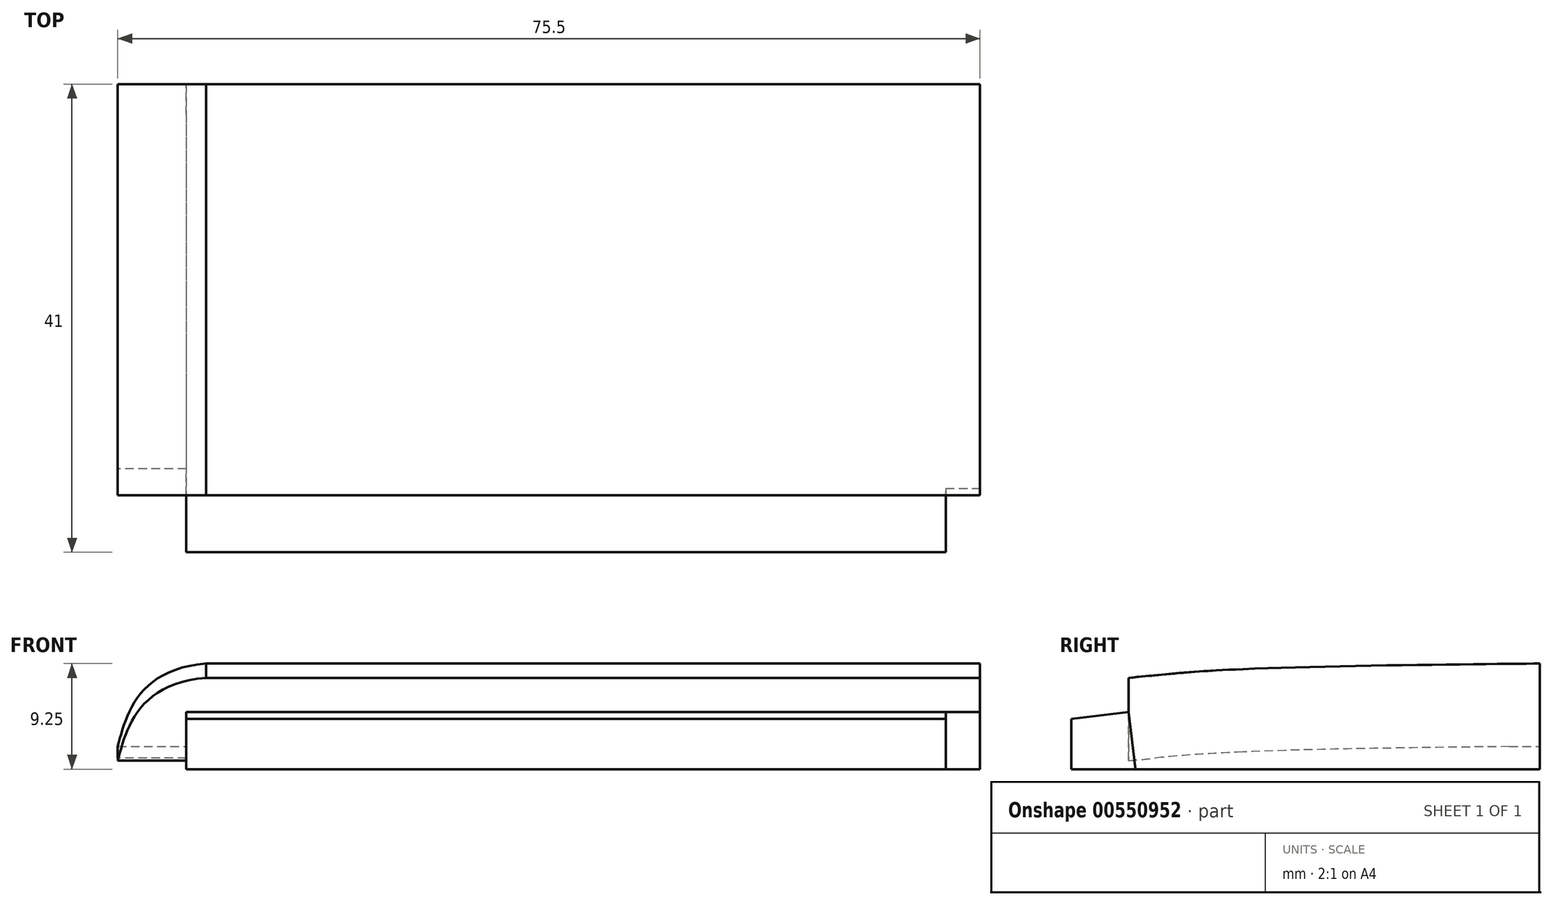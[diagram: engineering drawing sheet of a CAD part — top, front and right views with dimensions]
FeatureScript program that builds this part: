
annotation { "Feature Type Name" : "Feature", "Feature Type Description" : "" }
export const myFeature = defineFeature(function(context is Context, id is Id, definition is map)
    precondition{}
    {
        {
            var Q0;
            Q0=qCreatedBy(makeId("Right.planeOp"),FACE);
            var sketch = newSketch(context, id + "F0", { "sketchPlane" : qUnion([Q0])});
            skLineSegment(sketch, "E0", {"start": v(18, 0) * mm, "end": v(-18, 0) * mm});
            skLineSegment(sketch, "E1", {"start": v(18, 0) * mm, "end": v(18, 3) * mm});
            skLineSegment(sketch, "E2", {"start": v(-18, 0) * mm, "end": v(-18, 3) * mm});
            skLineSegment(sketch, "E3", {"start": v(-8, 0) * mm, "end": v(-8, 3.76) * mm});
            skLineSegment(sketch, "E4", {"start": v(18, 3) * mm, "end": v(18, 4.25) * mm});
            skFitSpline(sketch, "E5", {"points": [v(-18, 3) * mm, v(-8, 3.76) * mm, v(18, 4.25) * mm], "startDerivative": vector(22.72, 2.06) * mm, "endDerivative": vector(17.15, 0.15) * mm});
            skLineSegment(sketch, "E6.bottom", {"start": v(18, 0) * mm, "end": v(-23, 0) * mm});
            skLineSegment(sketch, "E6.top", {"start": v(18, -5) * mm, "end": v(-23, -5) * mm});
            skLineSegment(sketch, "E6.left", {"start": v(18, 0) * mm, "end": v(18, -5) * mm});
            skLineSegment(sketch, "E6.right", {"start": v(-23, 0) * mm, "end": v(-23, -5) * mm});
            skLineSegment(sketch, "E7", {"start": v(-18, 0) * mm, "end": v(-23, -0.6) * mm});
            skSolve(sketch);
        }
        {
            var Q0;
            {var subQ1=sQuery(id+"F0.wireOp",EDGE,"E1");Q0=makeQuery(id+"F0.imprint","IMPRINT",FACE,{"disambiguationData":[TD([[makeQuery(id+"F0.imprint","IMPRINT",EDGE,{"derivedFrom":subQ1}),1.0]])]});}
            var Q1;
            {var subQ0=sQuery(id+"F0.wireOp",EDGE,"E2");Q1=makeQuery(id+"F0.imprint","IMPRINT",FACE,{"disambiguationData":[TD([[makeQuery(id+"F0.imprint","IMPRINT",EDGE,{"derivedFrom":subQ0}),-1.0]])]});}
            var Q2;
            {var subQ1=sQuery(id+"F0.wireOp",EDGE,"E6.top");Q2=makeQuery(id+"F0.imprint","IMPRINT",FACE,{"disambiguationData":[TD([[makeQuery(id+"F0.imprint","IMPRINT",EDGE,{"derivedFrom":subQ1}),-1.0]])]});}
            extrude(context, id + "F1", {"entities" : qUnion([Q0, Q1, Q2]), "endBound" : BoundingType.SYMMETRIC, "depth" : 75.5 * mm, "offsetDistance" : 25 * mm});
        }
        {
            var Q0;
            Q0=makeQuery(id+"F1.opExtrude","SWEPT_FACE",FACE,{"disambiguationData":[OSD([sQuery(id+"F0.wireOp",EDGE,"E1"),sQuery(id+"F0.wireOp",EDGE,"E4"),sQuery(id+"F0.wireOp",EDGE,"E6.left")])]});
            var sketch = newSketch(context, id + "F2", { "sketchPlane" : qUnion([Q0])});
            skLineSegment(sketch, "E8.0", {"start": v(37.75, -5) * mm, "end": v(37.75, 4.25) * mm});
            skLineSegment(sketch, "E9.0", {"start": v(-37.75, 4.25) * mm, "end": v(37.75, 4.25) * mm});
            skPoint(sketch, "E10", {"position": v(30, 4.25) * mm});
            skPoint(sketch, "E11", {"position": v(37.75, -3) * mm});
            skFitSpline(sketch, "E12", {"points": [v(30, 4.25) * mm, v(37.75, -3) * mm], "startDerivative": vector(18.2, -1.34) * mm, "endDerivative": vector(2.03, -7.72) * mm});
            skSolve(sketch);
        }
        {
            var Q0;
            {var subQ3=sQuery(id+"F2.wireOp",EDGE,"E12");Q0=makeQuery(id+"F2.imprint","IMPRINT",FACE,{"disambiguationData":[TD([[makeQuery(id+"F2.imprint","IMPRINT",EDGE,{"derivedFrom":subQ3}),1.0]])]});}
            var Q1;
            Q1=makeQuery(id+"F1.opExtrude","CAP_EDGE",EDGE,{"disambiguationData":[OSD([sQuery(id+"F0.wireOp",EDGE,"E5")])],"isStart":true});
            sweep(context, id + "F3", {"operationType" : NewBodyOperationType.REMOVE, "profiles" : qUnion([Q0]), "path" : qUnion([Q1]), "keepProfileOrientation" : true});
        }
        {
            var Q0;
            Q0=makeQuery(id+"F1.opExtrude","CAP_FACE",FACE,{"disambiguationData":[OSD([sQuery(id+"F0.wireOp",EDGE,"E1"),sQuery(id+"F0.wireOp",EDGE,"E2"),sQuery(id+"F0.wireOp",EDGE,"E4"),sQuery(id+"F0.wireOp",EDGE,"E5"),sQuery(id+"F0.wireOp",EDGE,"E6.top"),sQuery(id+"F0.wireOp",EDGE,"E6.left"),sQuery(id+"F0.wireOp",EDGE,"E6.right"),sQuery(id+"F0.wireOp",EDGE,"E7")])],"isStart":true});
            var sketch = newSketch(context, id + "F4", { "sketchPlane" : qUnion([Q0])});
            skLineSegment(sketch, "E13.0.0", {"start": v(23, -0.6) * mm, "end": v(18, 0) * mm});
            skLineSegment(sketch, "E13.0.1", {"start": v(18, 0) * mm, "end": v(18, -4.25) * mm});
            skFitSpline(sketch, "E13.0.2", {"points": [v(18, -4.25) * mm, v(16.1, -4.08) * mm, v(14.5, -3.9) * mm, v(11.13, -3.65) * mm, v(9.86, -3.57) * mm, v(6.75, -3.43) * mm, v(4.92, -3.37) * mm, v(-4.98, -3.11) * mm, v(-15.14, -3.03) * mm, v(-18, -3) * mm]});
            skLineSegment(sketch, "E13.0.3", {"start": v(-18, -3) * mm, "end": v(-18, -5) * mm});
            skLineSegment(sketch, "E13.0.4", {"start": v(-18, -5) * mm, "end": v(23, -5) * mm});
            skLineSegment(sketch, "E13.0.5", {"start": v(23, -5) * mm, "end": v(23, -0.6) * mm});
            skSolve(sketch);
        }
        {
            var Q0;
            Q0=makeQuery(id+"F4.imprint","IMPRINT",FACE,{"disambiguationData":[TD([[makeQuery(id+"F4.imprint","IMPRINT",EDGE,{"derivedFrom":sQuery(id+"F4.wireOp",EDGE,"E13.0.0")}),-1.0]])]});
            extrude(context, id + "F5", {"entities" : qUnion([Q0]), "operationType" : NewBodyOperationType.REMOVE, "oppositeDirection" : true, "depth" : 6 * mm, "offsetDistance" : 25 * mm});
        }
        {
            var Q0;
            Q0=makeQuery(id+"F1.opExtrude","SWEPT_FACE",FACE,{"disambiguationData":[OSD([sQuery(id+"F0.wireOp",EDGE,"E7")])]});
            var sketch = newSketch(context, id + "F6", { "sketchPlane" : qUnion([Q0])});
            skLineSegment(sketch, "E14.bottom", {"start": v(37.75, -17.87) * mm, "end": v(34.75, -17.87) * mm});
            skLineSegment(sketch, "E14.top", {"start": v(37.75, -22.9) * mm, "end": v(34.75, -22.9) * mm});
            skLineSegment(sketch, "E14.left", {"start": v(37.75, -17.87) * mm, "end": v(37.75, -22.9) * mm});
            skLineSegment(sketch, "E14.right", {"start": v(34.75, -17.87) * mm, "end": v(34.75, -22.9) * mm});
            skSolve(sketch);
        }
        {
            var Q0;
            Q0=makeQuery(id+"F6.imprint","IMPRINT",FACE,{"disambiguationData":[TD([[makeQuery(id+"F6.imprint","IMPRINT",EDGE,{"derivedFrom":sQuery(id+"F6.wireOp",EDGE,"E14.bottom")}),1.0]])]});
            extrude(context, id + "F7", {"entities" : qUnion([Q0]), "operationType" : NewBodyOperationType.REMOVE, "oppositeDirection" : true, "depth" : 25 * mm, "offsetDistance" : 25 * mm});
        }
        {
            var Q0;
            Q0=makeQuery(id+"F1.opExtrude","SWEPT_FACE",FACE,{"disambiguationData":[OSD([sQuery(id+"F0.wireOp",EDGE,"E6.right")])]});
            var sketch = newSketch(context, id + "F8", { "sketchPlane" : qUnion([Q0])});
            skLineSegment(sketch, "E15.bottom", {"start": v(37.75, -5) * mm, "end": v(34.75, -5) * mm});
            skLineSegment(sketch, "E15.top", {"start": v(37.75, -0.6) * mm, "end": v(34.75, -0.6) * mm});
            skLineSegment(sketch, "E15.left", {"start": v(37.75, -5) * mm, "end": v(37.75, -0.6) * mm});
            skLineSegment(sketch, "E15.right", {"start": v(34.75, -5) * mm, "end": v(34.75, -0.6) * mm});
            skSolve(sketch);
        }
        {
            var Q0;
            Q0=makeQuery(id+"F8.imprint","IMPRINT",FACE,{"disambiguationData":[TD([[makeQuery(id+"F8.imprint","IMPRINT",EDGE,{"derivedFrom":sQuery(id+"F8.wireOp",EDGE,"E15.bottom")}),-1.0]])]});
            extrude(context, id + "F9", {"entities" : qUnion([Q0]), "operationType" : NewBodyOperationType.REMOVE, "endBound" : BoundingType.UP_TO_NEXT, "oppositeDirection" : true, "depth" : 25 * mm, "offsetDistance" : 25 * mm});
        }
    });
